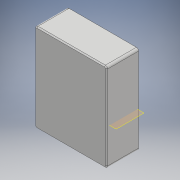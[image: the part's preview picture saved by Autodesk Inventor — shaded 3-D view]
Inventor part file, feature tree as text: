
AUTODESK INVENTOR PART (.ipt)
format: ipt  version: 2017 (Build 210142000, 142)  size: 277,504 bytes
history: native  units: mm
features: projected_geometry x8, sketch x6, extrude x4, other x1, chamfer x1, plane x1, sweep x1
ambient origin geometry x8: Origin, YZ Plane, XZ Plane, XY Plane, X Axis, Y Axis, Z Axis, Center Point
bodies: Solid1 (feature_tree)
feature tree (22):
  extrude  "Extrusion1"  Depth=80.0mm
  extrude  "Extrusion2"  Depth=3.0mm TaperAngle=0.0deg
  extrude  "Extrusion3"  Depth=53.3mm
  other  "Lip1"
  extrude  "Extrusion4"  Depth=5.0mm
  chamfer  "Chamfer2"  Distance=5.1mm
  plane  "Work Plane1"
  sweep  "Sweep1"
  sketch  "Sketch1"  dims[d0=65.0mm d1=80.0mm]
  sketch  "Sketch2"  dims[d2=2.0mm d3=3.0mm d4=0.0mm]
  projected_geometry  "Projected Loop1"
  sketch  "Sketch3"  dims[d5=68.6mm d6=53.3mm]
  projected_geometry  "Projected Loop2"
  sketch  "Sketch4"  dims[d7=5.0mm d8=15.2mm]
  projected_geometry  "Projected Loop3"
  sketch  "Sketch7"  dims[d9=27.9mm d10=5.1mm d11=50.8mm d12=1.3mm d13=14.0mm d14=2.5mm d15=2.5mm d17=6.0mm d18=2.0mm d19=0.0mm d20=3.0mm d21=2.0mm d22=26.0mm d23=0.0mm d27=3.0mm d28=1.0mm d29=0.0mm d30=0.0mm d31=0.0mm d32=0.0mm d33=6.9mm d34=12.0mm d35=1.6mm d36=11.0mm d37=7.4mm d38=26.5mm d39=14.5mm d40=17.4mm d41=1.85mm d42=9.0mm d43=1.6mm d44=11.0mm d45=28.0mm d46=0.0mm d47=1.0mm d48=2.0mm d49=45.0deg d50=30.0mm d53=10.0mm d54=1.0mm d57=0.5mm d58=0.0mm d59=0.0mm]
  projected_geometry  "Projected Loop5"
  projected_geometry  "Projected Loop6"
  projected_geometry  "Projected Loop7"
  projected_geometry  "Projected Loop8"
  projected_geometry  "Projected Loop9"
  sketch  "3D Sketch1"
